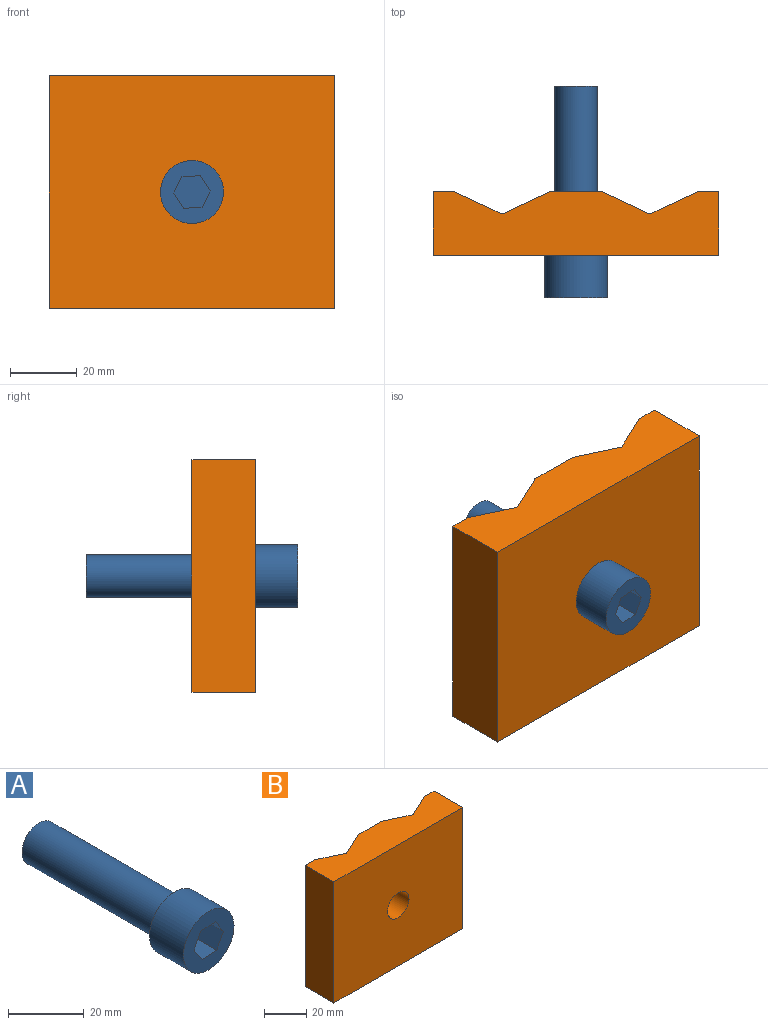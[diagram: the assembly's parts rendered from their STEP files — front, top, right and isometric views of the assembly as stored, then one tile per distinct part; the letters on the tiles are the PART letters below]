
ASSEMBLY  parts=2 mates=1
PART A: 12 faces, bbox 19.3x63.5x19.2 mm
  f0: plane 12.92x12.92mm, normal (0,1,0), area 126.7mm2, adj f1
  f1: cylinder r=6.35mm len=50.8mm, axis (0,-1,0), area 2026.8mm2, adj f0,f2
  f2: plane 19.25x19.25mm, normal (0,1,0), area 154.6mm2, adj f1,f3
  f3: cylinder r=9.46mm len=18.92mm, axis (0,-1,0), area 755mm2, adj f2,f8
  f4: plane 9.53x5.49mm, normal (0.06,0,-1), area 52.4mm2, adj f5,f7,f8,f10
  f5: plane 9.53x4.91mm, normal (0.89,0,-0.45), area 52.4mm2, adj f4,f6,f8,f10
  f6: plane 9.53x4.6mm, normal (0.84,0,0.55), area 52.4mm2, adj f5,f8,f9,f10
  f7: plane 9.53x4.6mm, normal (-0.84,0,-0.55), area 52.4mm2, adj f4,f8,f10,f11
  f8: plane 19.25x19.25mm, normal (0,-1,0), area 202.7mm2, adj f3,f4,f5,f6,f7,f9,f11
  f9: plane 9.53x5.49mm, normal (-0.06,0,1), area 52.4mm2, adj f6,f8,f10,f11
  f10: plane 10.98x9.81mm, normal (0,-1,0), area 78.6mm2, adj f4,f5,f6,f7,f9,f11
  f11: plane 9.53x4.91mm, normal (-0.89,0,0.45), area 52.4mm2, adj f7,f8,f9,f10
PART B: 13 faces, bbox 85.7x19.1x69.9 mm
  f0: plane 69.85x6.35mm, normal (0,1,0), area 443.5mm2, adj f3,f4,f6,f8
  f1: plane 69.85x14.29mm, normal (0.42,0.91,0), area 1101.2mm2, adj f2,f6,f7,f8
  f2: plane 69.85x6.35mm, normal (0,1,0), area 443.5mm2, adj f1,f5,f6,f8
  f3: plane 69.85x14.29mm, normal (-0.42,0.91,0), area 1101.2mm2, adj f0,f6,f8,f9
  f4: plane 69.85x19.05mm, normal (1,0,0), area 1330.6mm2, adj f0,f6,f8,f10
  f5: plane 69.85x19.05mm, normal (-1,0,0), area 1330.6mm2, adj f2,f6,f8,f10
  f6: plane 85.73x19.05mm, normal (0,0,-1), area 1442.7mm2, adj f0,f1,f2,f3,f4,f5,f7,f9
  f7: plane 69.85x14.29mm, normal (-0.42,0.91,0), area 1101.2mm2, adj f1,f6,f8,f11
  f8: plane 85.73x19.05mm, normal (0,0,1), area 1442.7mm2, adj f0,f1,f2,f3,f4,f5,f7,f9
  f9: plane 69.85x14.29mm, normal (0.42,0.91,0), area 1101.2mm2, adj f3,f6,f8,f11
  f10: plane 85.73x69.85mm, normal (0,-1,0), area 5827.6mm2, adj f4,f5,f6,f8,f12
  f11: plane 69.85x15.88mm, normal (0,1,0), area 948.5mm2, adj f6,f7,f8,f9,f12
  f12: cylinder r=7.14mm len=19.05mm, axis (0,-1,0), area 855.1mm2, adj f10,f11
PLACE A rot(axis=(-0.99,0.13,-0.02),0deg) t=(177.8,68.68,0)mm
PLACE B t=(88.9,68.68,0)mm fixed
MATE fastened A.f1 <-> B.f12  axis (0,1,0) through (0,0,0)mm
